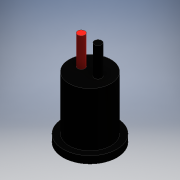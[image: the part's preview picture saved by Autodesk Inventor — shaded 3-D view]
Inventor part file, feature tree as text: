
AUTODESK INVENTOR PART (.ipt)
format: ipt  version: 2016 (Build 200138000, 138)  size: 143,360 bytes
history: native  units: mm
features: extrude x4, sketch x4
ambient origin geometry x8: Origin, YZ Plane, XZ Plane, XY Plane, X Axis, Y Axis, Z Axis, Center Point
bodies: Solid1 (feature_tree)
feature tree (8):
  extrude  "Extrusion1"  Depth=37.0mm TaperAngle=0.0deg
  extrude  "Extrusion2"  Depth=5.0mm
  extrude  "Extrusion3"  Depth=37.0mm
  extrude  "Extrusion4"  Depth=4.0mm
  sketch  "Sketch1"  dims[d0=28.78mm d1=37.0mm d2=0.0mm]
  sketch  "Sketch2"  dims[d3=5.0mm d4=5.0mm]
  sketch  "Sketch3"  dims[d5=20.0mm d6=0.0mm d7=37.0mm]
  sketch  "Sketch4"  dims[d8=5.0mm d9=0.0mm d10=4.0mm d11=14.0mm d12=14.0mm d13=4.0mm d14=2.0mm d15=0.0mm]
